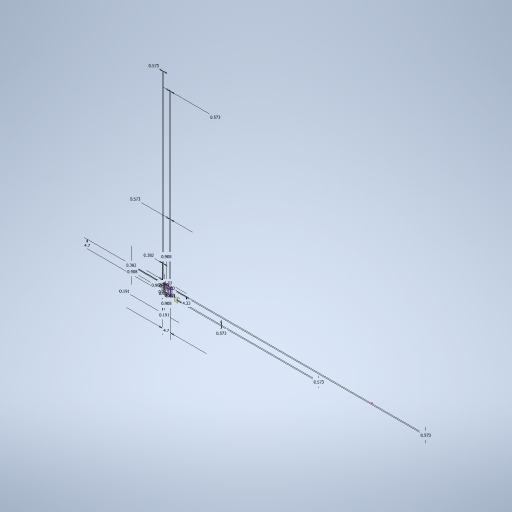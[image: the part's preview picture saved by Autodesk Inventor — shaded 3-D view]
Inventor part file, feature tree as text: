
AUTODESK INVENTOR PART (.ipt)
format: ipt  version: 2024 (Build 280153000, 153)  size: 352,768 bytes
history: native  units: in
note: dims shown in document units (in); Inventor stores cm internally (conversion verified against a paired STEP export)
features: extrude x4, fillet x2, plane x1, sketch x1
ambient origin geometry x8: Origin, YZ Plane, XZ Plane, XY Plane, X Axis, Y Axis, Z Axis, Center Point
bodies: Body1 (feature_tree)
feature tree (8):
  plane  "Work Plane3"
  sketch  "Sketch1"  dims[d1=1.8504in d2=1.8504in d4=0.1035in d5=0.2257in d6=0.0752in d7=0.0752in d8=1.7047in d9=1.7047in d10=0.1035in d11=0.1505in d12=0.2257in d13=0.2257in d14=0.1035in d15=0.2257in d16=0.2257in d17=0.1035in d18=0.2257in d19=0.1505in d20=0.2445in d21=0.2445in d22=0.2445in d23=0.2445in d24=0.3574in d25=0.3574in d26=0.3574in d27=0.3574in d32=0.315in d33=0.0in d45=0.3937in d46=0.0in d47=0.1575in d48=0.0in d51=0.1181in d52=0.0in d55=0.3937in d56=0.0787in]
  extrude  "Extrusion3"  Depth=1.8504in
  extrude  "Extrusion6"  Depth=0.0787in
  extrude  "Extrusion7"  Depth=0.0787in
  extrude  "Extrusion8"  Depth=0.0752in
  fillet  "Fillet5"  Radius=0.0752in
  fillet  "Fillet6"  Radius=1.7047in
